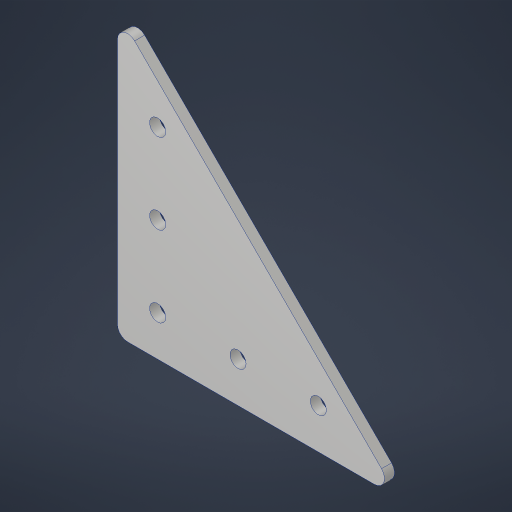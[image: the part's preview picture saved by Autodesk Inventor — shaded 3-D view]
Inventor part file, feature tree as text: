
AUTODESK INVENTOR PART (.ipt)
format: ipt  version: 2023.4 (Build 274418000, 418)  size: 188,928 bytes
history: native  units: in
note: dims shown in document units (in); Inventor stores cm internally (conversion verified against a paired STEP export)
features: pattern_linear x2, sketch x2, extrude x1, fillet x1, hole x1, projected_geometry x1
ambient origin geometry x8: Origin, YZ Plane, XZ Plane, XY Plane, X Axis, Y Axis, Z Axis, Center Point
bodies: Solid1 (feature_tree)
feature tree (8):
  extrude  "Extrusion1"  Depth=3.5in
  fillet  "Fillet1"  Radius=0.125in
  hole  "Hole1"  [1 undecoded]
  pattern_linear  "Rectangular Pattern1"  Spacing1=0.5in  [1 undecoded]
  pattern_linear  "Rectangular Pattern2"  Count1=3 Spacing1=1.0in
  sketch  "Sketch1"  dims[d0=3.5in d1=3.5in d2=0.125in d3=0.0in]
  sketch  "Sketch2"  dims[d4=0.125in d5=0.5in d6=0.5in d7=0.201in d8=0.75in d9=0.385in d10=0.25in d11=0.5635in d12=1.0in d13=0.8108in d14=1.1811in d16=1.0in d17=1.1811in d19=1.0in]
  projected_geometry  "Project Cut Edges1"
note: 2 required parameter values undecoded (feature->parameter linkage not recoverable at this tier; creation-order binding heuristic only, values carry confidence <= 0.55)
